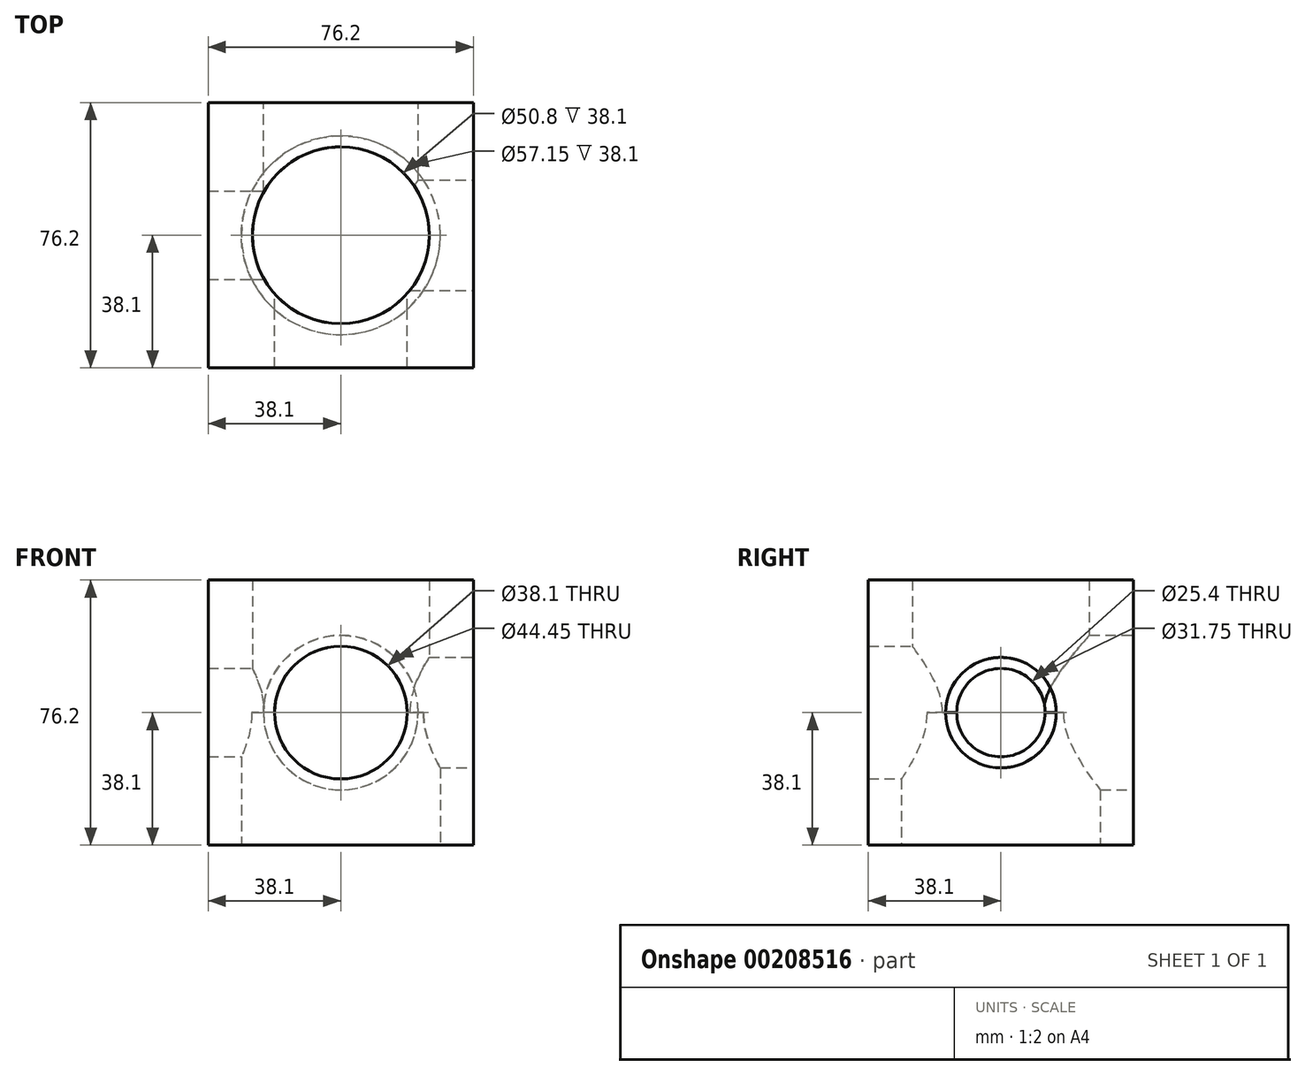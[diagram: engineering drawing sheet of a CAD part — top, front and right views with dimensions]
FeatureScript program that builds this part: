
annotation { "Feature Type Name" : "Feature", "Feature Type Description" : "" }
export const myFeature = defineFeature(function(context is Context, id is Id, definition is map)
    precondition{}
    {
        {
            var Q0;
            Q0=qCreatedBy(makeId("Front.planeOp"),FACE);
            var sketch = newSketch(context, id + "F0", { "sketchPlane" : qUnion([Q0])});
            skLineSegment(sketch, "E0.bottom", {"start": v(38.1, 38.1) * mm, "end": v(-38.1, 38.1) * mm});
            skLineSegment(sketch, "E0.top", {"start": v(38.1, -38.1) * mm, "end": v(-38.1, -38.1) * mm});
            skLineSegment(sketch, "E0.left", {"start": v(38.1, 38.1) * mm, "end": v(38.1, -38.1) * mm});
            skLineSegment(sketch, "E0.right", {"start": v(-38.1, 38.1) * mm, "end": v(-38.1, -38.1) * mm});
            skPoint(sketch, "E0.middle", {"position": v(0, 0) * mm});
            skCircle(sketch, "E1", {"center": v(0, 0) * mm, "radius": 19.05 * mm});
            skSolve(sketch);
        }
        {
            var Q0;
            Q0=makeQuery(id+"F0.imprint","IMPRINT",FACE,{"disambiguationData":[TD([[makeQuery(id+"F0.imprint","IMPRINT",EDGE,{"derivedFrom":sQuery(id+"F0.wireOp",EDGE,"E0.bottom")}),1.0]])]});
            extrude(context, id + "F1", {"entities" : qUnion([Q0]), "depth" : 76.2 * mm});
        }
        {
            var Q0;
            Q0=makeQuery(id+"F1.opExtrude","SWEPT_FACE",FACE,{"disambiguationData":[OSD([sQuery(id+"F0.wireOp",EDGE,"E0.left")])]});
            var sketch = newSketch(context, id + "F2", { "sketchPlane" : qUnion([Q0])});
            skCircle(sketch, "E2", {"center": v(-38.1, 0) * mm, "radius": 12.7 * mm});
            skPoint(sketch, "E2.centerSnap0", {"position": v(-38.1, 38.1) * mm});
            skPoint(sketch, "E2.centerSnap1", {"position": v(-76.2, 0) * mm});
            skSolve(sketch);
        }
        {
            var Q0;
            Q0=makeQuery(id+"F2.imprint","IMPRINT",FACE,{"disambiguationData":[TD([[makeQuery(id+"F2.imprint","IMPRINT",EDGE,{"derivedFrom":sQuery(id+"F2.wireOp",EDGE,"E2")}),1.0]])]});
            extrude(context, id + "F3", {"entities" : qUnion([Q0]), "operationType" : NewBodyOperationType.REMOVE, "oppositeDirection" : true, "depth" : 76.2 * mm});
        }
        {
            var Q0;
            Q0=makeQuery(id+"F1.opExtrude","SWEPT_FACE",FACE,{"disambiguationData":[OSD([sQuery(id+"F0.wireOp",EDGE,"E0.top")])]});
            var sketch = newSketch(context, id + "F4", { "sketchPlane" : qUnion([Q0])});
            skCircle(sketch, "E3", {"center": v(0, 38.1) * mm, "radius": 25.4 * mm});
            skPoint(sketch, "E3.centerSnap0", {"position": v(-38.1, 38.1) * mm});
            skSolve(sketch);
        }
        {
            var Q0;
            Q0=makeQuery(id+"F4.imprint","IMPRINT",FACE,{"disambiguationData":[TD([[makeQuery(id+"F4.imprint","IMPRINT",EDGE,{"derivedFrom":sQuery(id+"F4.wireOp",EDGE,"E3")}),1.0]])]});
            extrude(context, id + "F5", {"entities" : qUnion([Q0]), "operationType" : NewBodyOperationType.REMOVE, "oppositeDirection" : true, "depth" : 76.2 * mm});
        }
        {
            var Q0;
            Q0=makeQuery(id+"F1.opExtrude","CAP_FACE",FACE,{"disambiguationData":[OSD([sQuery(id+"F0.wireOp",EDGE,"E0.bottom"),sQuery(id+"F0.wireOp",EDGE,"E0.top"),sQuery(id+"F0.wireOp",EDGE,"E0.left"),sQuery(id+"F0.wireOp",EDGE,"E0.right"),sQuery(id+"F0.wireOp",EDGE,"E1")])],"isStart":true});
            var sketch = newSketch(context, id + "F6", { "sketchPlane" : qUnion([Q0])});
            skCircle(sketch, "E4", {"center": v(0, 0) * mm, "radius": 22.23 * mm});
            skSolve(sketch);
        }
        {
            var Q0;
            Q0=makeQuery(id+"F6.imprint","IMPRINT",FACE,{"disambiguationData":[TD([[makeQuery(id+"F6.imprint","IMPRINT",EDGE,{"derivedFrom":sQuery(id+"F6.wireOp",EDGE,"E4")}),1.0]])]});
            extrude(context, id + "F7", {"entities" : qUnion([Q0]), "operationType" : NewBodyOperationType.REMOVE, "oppositeDirection" : true, "depth" : 38.1 * mm});
        }
        {
            var Q0;
            Q0=makeQuery(id+"F1.opExtrude","SWEPT_FACE",FACE,{"disambiguationData":[OSD([sQuery(id+"F0.wireOp",EDGE,"E0.top")])]});
            var sketch = newSketch(context, id + "F8", { "sketchPlane" : qUnion([Q0])});
            skCircle(sketch, "E5", {"center": v(0, 38.1) * mm, "radius": 28.58 * mm});
            skSolve(sketch);
        }
        {
            var Q0;
            Q0=makeQuery(id+"F8.imprint","IMPRINT",FACE,{"disambiguationData":[TD([[makeQuery(id+"F8.imprint","IMPRINT",EDGE,{"derivedFrom":sQuery(id+"F8.wireOp",EDGE,"E5")}),1.0]])]});
            extrude(context, id + "F9", {"entities" : qUnion([Q0]), "operationType" : NewBodyOperationType.REMOVE, "oppositeDirection" : true, "depth" : 38.1 * mm});
        }
        {
            var Q0;
            Q0=makeQuery(id+"F1.opExtrude","SWEPT_FACE",FACE,{"disambiguationData":[OSD([sQuery(id+"F0.wireOp",EDGE,"E0.left")])]});
            var sketch = newSketch(context, id + "F10", { "sketchPlane" : qUnion([Q0])});
            skCircle(sketch, "E6", {"center": v(-38.1, 0) * mm, "radius": 15.88 * mm});
            skSolve(sketch);
        }
        {
            var Q0;
            Q0=makeQuery(id+"F10.imprint","IMPRINT",FACE,{"disambiguationData":[TD([[makeQuery(id+"F10.imprint","IMPRINT",EDGE,{"derivedFrom":sQuery(id+"F10.wireOp",EDGE,"E6")}),1.0]])]});
            extrude(context, id + "F11", {"entities" : qUnion([Q0]), "operationType" : NewBodyOperationType.REMOVE, "oppositeDirection" : true, "depth" : 38.1 * mm});
        }
    });
